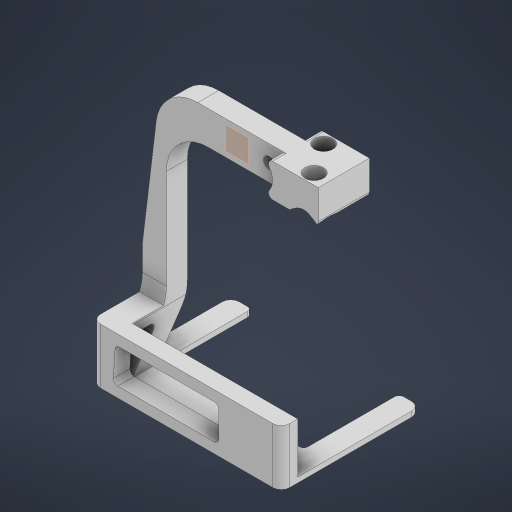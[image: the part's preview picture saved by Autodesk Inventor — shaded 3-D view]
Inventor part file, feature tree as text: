
AUTODESK INVENTOR PART (.ipt)
format: ipt  version: 2024.1 (Build 281209000, 209)  size: 319,488 bytes
history: native  units: in
note: dims shown in document units (in); Inventor stores cm internally (conversion verified against a paired STEP export)
features: other x3, sketch x1, plane x1
ambient origin geometry x8: Origin, YZ Plane, XZ Plane, XY Plane, X Axis, Y Axis, Z Axis, Center Point
bodies: Solid1 (feature_tree)
feature tree (5):
  other  "Leg.ipt"
  other  "Solid1::Leg.ipt"
  other  "TaggingFeature1"
  sketch  "Sketch3"  dims[d0=0.3937in]
  plane  "Work Plane1"
